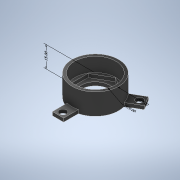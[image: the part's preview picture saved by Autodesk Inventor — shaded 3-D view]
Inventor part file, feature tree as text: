
AUTODESK INVENTOR PART (.ipt)
format: ipt  version: 2022 (Build 260153000, 153)  size: 190,464 bytes
history: native  units: mm
features: extrude x5, sketch x5, other x4
ambient origin geometry x8: Origin, YZ Plane, XZ Plane, XY Plane, X Axis, Y Axis, Z Axis, Center Point
bodies: Solid1 (feature_tree)
feature tree (14):
  other  "Annotations"
  extrude  "Extrusion1"  Depth=33.0mm
  extrude  "Extrusion2"  Depth=2.5mm TaperAngle=0.0deg
  extrude  "Extrusion3"  Depth=2.5mm TaperAngle=0.0deg
  extrude  "Extrusion4"  Depth=10.0mm TaperAngle=0.0deg
  extrude  "Extrusion5"  TaperAngle=120.0deg  [1 undecoded]
  sketch  "Sketch1"  dims[d0=12.25mm d1=33.0mm]
  sketch  "Sketch2"  dims[d2=5.0mm d3=0.0mm d4=2.5mm d5=0.0mm]
  sketch  "Sketch3"  dims[d6=20.0mm d7=2.5mm d8=0.0mm]
  sketch  "Sketch4"  dims[d9=29.0mm d10=10.0mm d11=0.0mm]
  sketch  "Sketch5"  dims[d12=120.0deg d13=120.0deg d14=4.0mm d15=12.0mm d16=8.0mm d17=4.0mm d18=6.5mm d19=5.0mm d20=30.0mm d22=360.0deg d24=2.5mm d25=0.0mm d26=28.118715mm d27=29.0mm d28=31.029943mm d29=33.0mm d30=15.0mm]
  other  "Diameter Dimension 1"
  other  "Diameter Dimension 2"
  other  "Linear Dimension 1"
note: 1 required parameter value undecoded (feature->parameter linkage not recoverable at this tier; creation-order binding heuristic only, values carry confidence <= 0.55)
